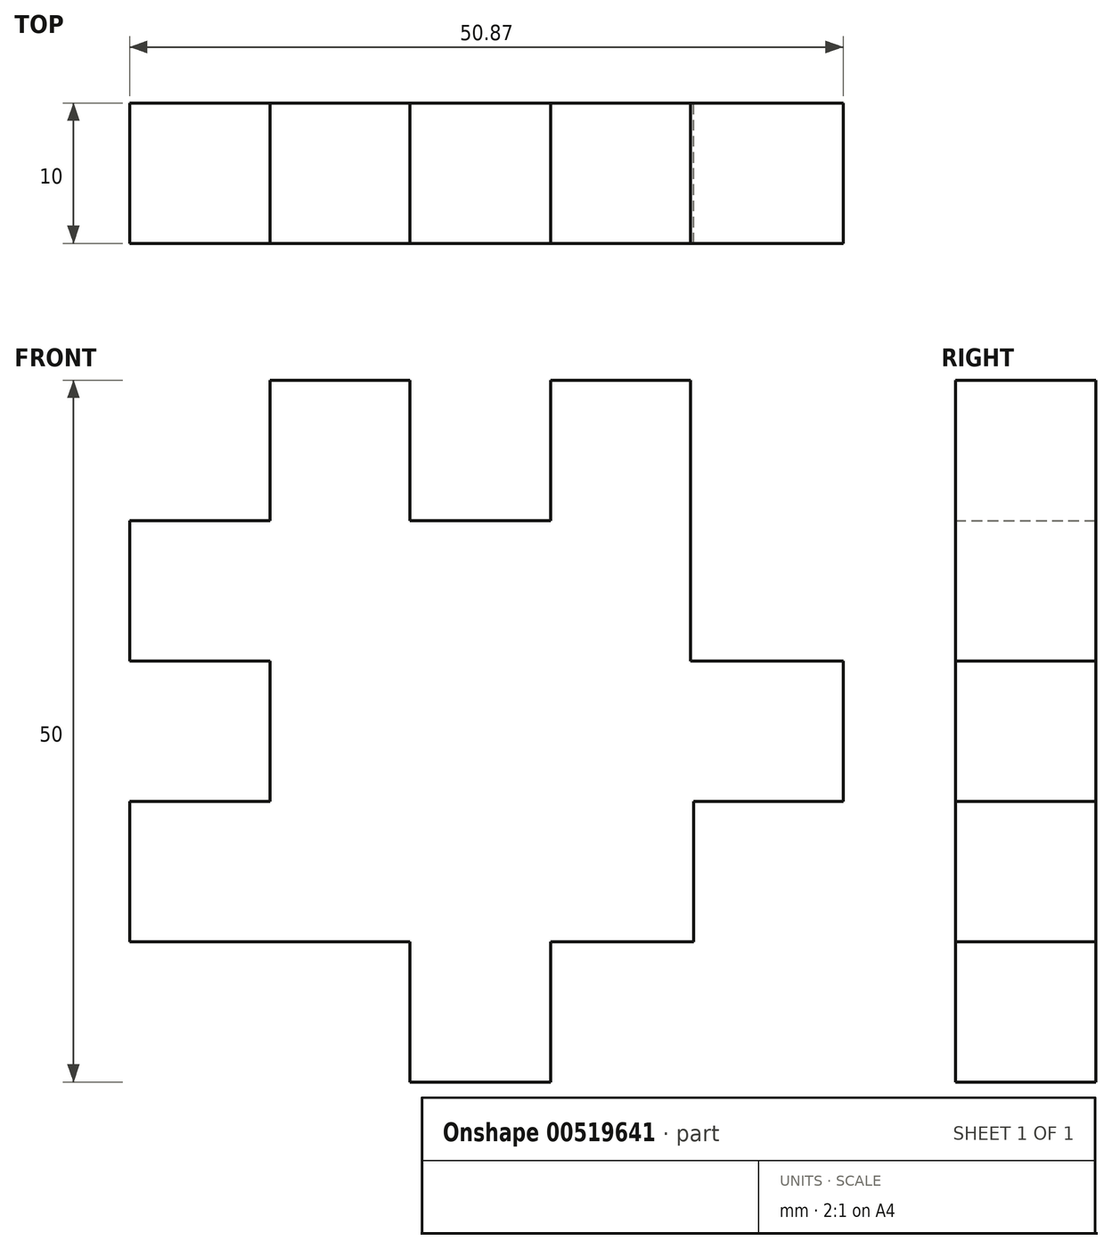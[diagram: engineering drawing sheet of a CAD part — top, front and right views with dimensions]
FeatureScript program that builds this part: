
annotation { "Feature Type Name" : "Feature", "Feature Type Description" : "" }
export const myFeature = defineFeature(function(context is Context, id is Id, definition is map)
    precondition{}
    {
        {
            var Q0;
            Q0=qCreatedBy(makeId("Front.planeOp"),FACE);
            var sketch = newSketch(context, id + "F0", { "sketchPlane" : qUnion([Q0])});
            skLineSegment(sketch, "E0", {"start": v(-50.87, 33.91) * mm, "end": v(-50.87, 23.91) * mm});
            skLineSegment(sketch, "E1", {"start": v(-50.87, 23.91) * mm, "end": v(-40.87, 23.91) * mm});
            skLineSegment(sketch, "E2", {"start": v(-40.87, 23.91) * mm, "end": v(-40.87, 13.91) * mm});
            skLineSegment(sketch, "E3", {"start": v(-40.87, 13.91) * mm, "end": v(-50.87, 13.91) * mm});
            skLineSegment(sketch, "E4", {"start": v(-50.87, 13.91) * mm, "end": v(-50.87, 3.91) * mm});
            skLineSegment(sketch, "E5", {"start": v(-50.87, 3.91) * mm, "end": v(-30.87, 3.91) * mm});
            skLineSegment(sketch, "E6", {"start": v(-30.87, 3.91) * mm, "end": v(-30.87, -6.09) * mm});
            skLineSegment(sketch, "E7", {"start": v(-30.87, -6.09) * mm, "end": v(-20.87, -6.09) * mm});
            skLineSegment(sketch, "E8", {"start": v(-20.87, 3.91) * mm, "end": v(-20.87, -6.09) * mm});
            skLineSegment(sketch, "E9", {"start": v(-20.87, 3.91) * mm, "end": v(-10.65, 3.91) * mm});
            skLineSegment(sketch, "E10", {"start": v(-10.65, 3.91) * mm, "end": v(-10.65, 13.91) * mm});
            skLineSegment(sketch, "E11", {"start": v(-10.65, 13.91) * mm, "end": v(0, 13.91) * mm});
            skLineSegment(sketch, "E12", {"start": v(0, 13.91) * mm, "end": v(0, 23.91) * mm});
            skLineSegment(sketch, "E13", {"start": v(0, 23.91) * mm, "end": v(-10.87, 23.91) * mm});
            skLineSegment(sketch, "E14", {"start": v(-10.87, 23.91) * mm, "end": v(-10.87, 43.91) * mm});
            skLineSegment(sketch, "E15", {"start": v(-10.87, 43.91) * mm, "end": v(-20.87, 43.91) * mm});
            skLineSegment(sketch, "E16", {"start": v(-20.87, 43.91) * mm, "end": v(-20.87, 33.91) * mm});
            skLineSegment(sketch, "E17", {"start": v(-20.87, 33.91) * mm, "end": v(-30.87, 33.91) * mm});
            skLineSegment(sketch, "E18", {"start": v(-30.87, 33.91) * mm, "end": v(-30.87, 43.91) * mm});
            skLineSegment(sketch, "E19", {"start": v(-30.87, 43.91) * mm, "end": v(-40.87, 43.91) * mm});
            skLineSegment(sketch, "E20", {"start": v(-40.87, 43.91) * mm, "end": v(-40.87, 33.91) * mm});
            skLineSegment(sketch, "E21", {"start": v(-40.87, 33.91) * mm, "end": v(-50.87, 33.91) * mm});
            skSolve(sketch);
        }
        {
            var Q0;
            Q0 = qSketchRegion(id + "F0", true);
            extrude(context, id + "F1", {"entities" : qUnion([Q0]), "depth" : 10 * mm, "offsetDistance" : 25 * mm});
        }
    });
